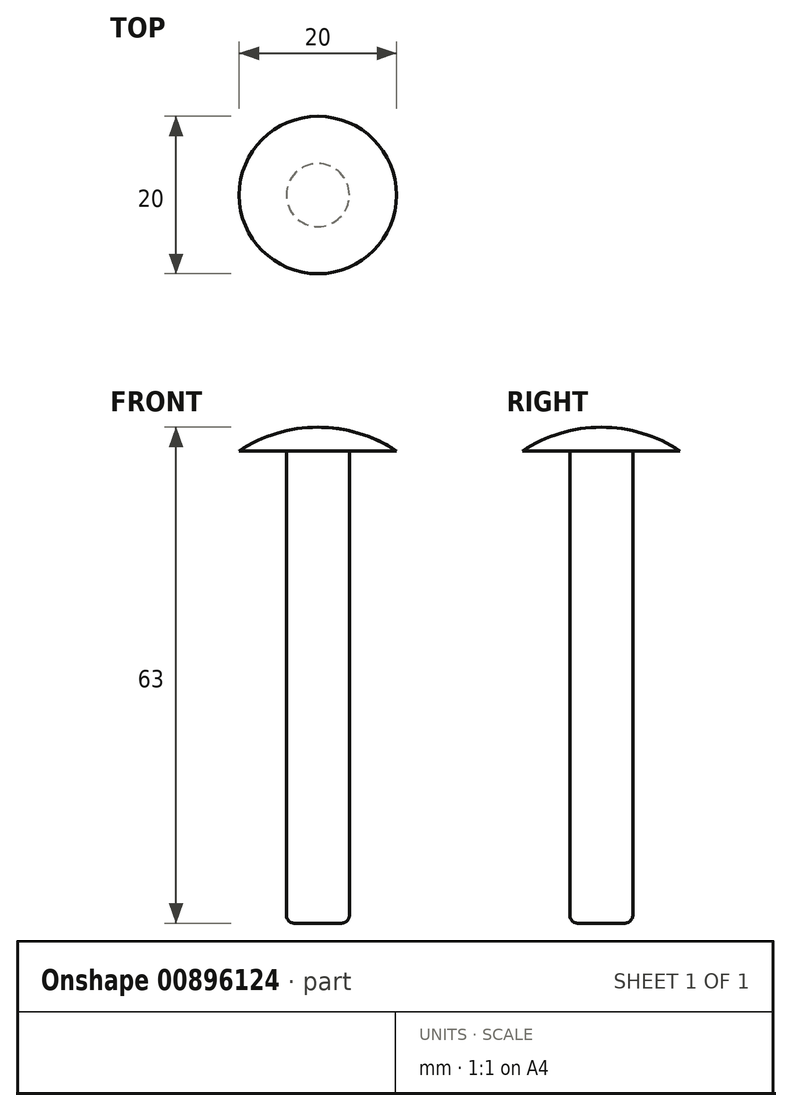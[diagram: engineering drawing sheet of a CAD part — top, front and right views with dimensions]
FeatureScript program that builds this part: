
annotation { "Feature Type Name" : "Feature", "Feature Type Description" : "" }
export const myFeature = defineFeature(function(context is Context, id is Id, definition is map)
    precondition{}
    {
        {
            var Q0;
            Q0=qCreatedBy(makeId("Front.planeOp"),FACE);
            var sketch = newSketch(context, id + "F0", { "sketchPlane" : qUnion([Q0])});
            skLineSegment(sketch, "E0", {"start": v(0, 0) * mm, "end": v(0, -60) * mm});
            skLineSegment(sketch, "E1", {"start": v(0, -60) * mm, "end": v(3, -60) * mm});
            skLineSegment(sketch, "E2", {"start": v(4, -59) * mm, "end": v(4, 0) * mm});
            skLineSegment(sketch, "E3", {"start": v(4, 0) * mm, "end": v(10, 0) * mm});
            skLineSegment(sketch, "E4", {"start": v(0, 3) * mm, "end": v(-23.12, 3) * mm, "construction": true});
            skArc(sketch, "E5", {"start": v(0, 3) * mm, "mid": v(5.22, 2.23) * mm, "end": v(10, 0) * mm});
            skLineSegment(sketch, "E6", {"start": v(0, 0) * mm, "end": v(0, 3) * mm});
            skLineSegment(sketch, "E7", {"start": v(0, -48.04) * mm, "end": v(0, -60) * mm, "construction": true});
            skPoint(sketch, "E8.visualSharp", {"position": v(4, -60) * mm});
            skArc(sketch, "E8.filletArc", {"start": v(3, -60) * mm, "mid": v(3.7, -59.7) * mm, "end": v(4, -59) * mm});
            skSolve(sketch);
        }
        {
            var Q0;
            Q0 = qSketchRegion(id + "F0", true);
            var Q1;
            Q1=sQuery(id+"F0.wireOp",EDGE,"E0");
            revolve(context, id + "F1", {"surfaceOperationType" : NewSurfaceOperationType.NEW, "entities" : qUnion([Q0]), "axis" : qUnion([Q1]), "revolveType" : RevolveType.FULL});
        }
    });
